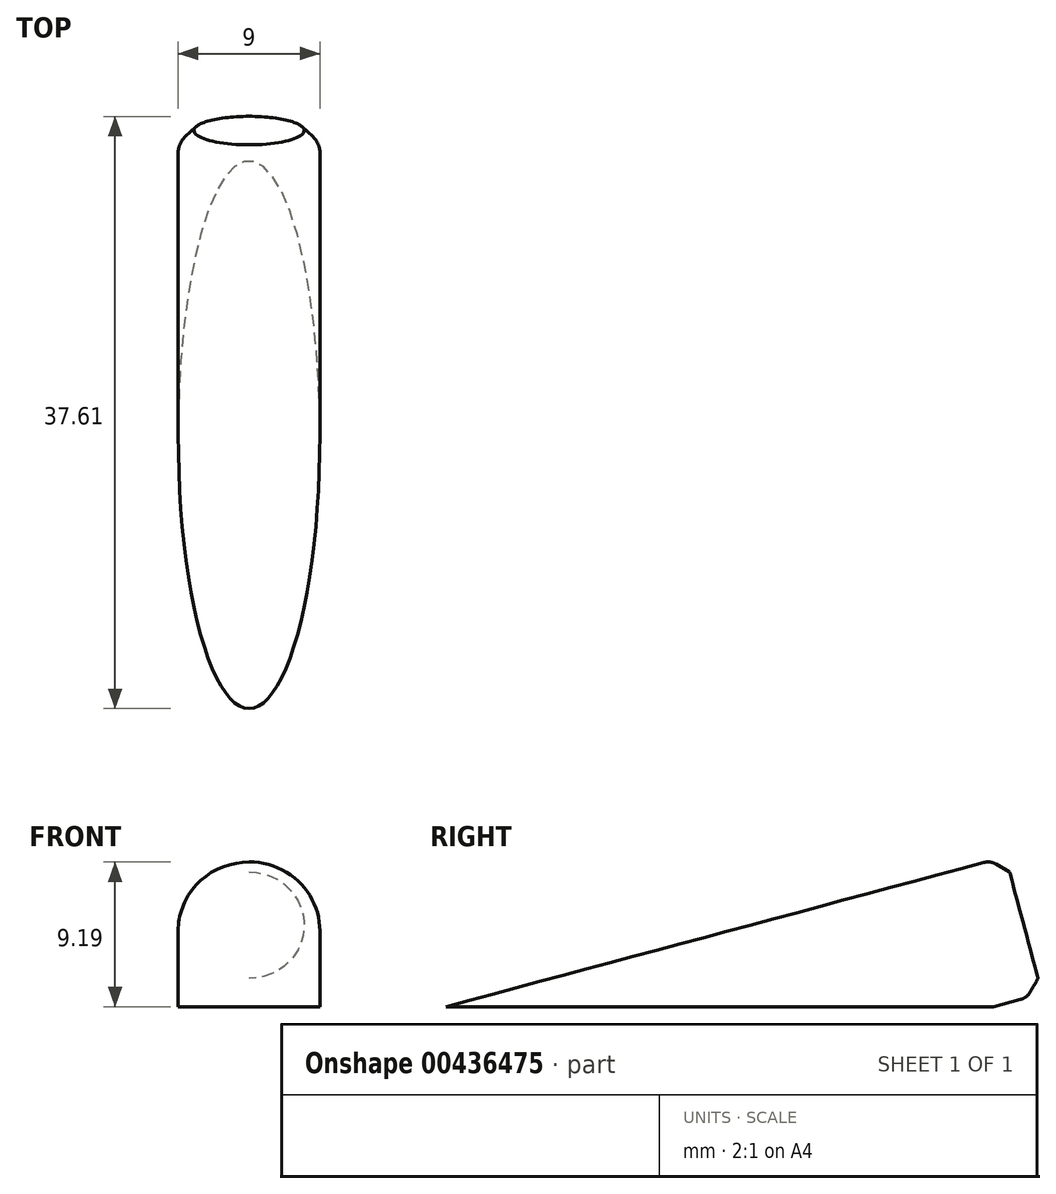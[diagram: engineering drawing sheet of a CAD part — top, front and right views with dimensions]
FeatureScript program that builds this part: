
annotation { "Feature Type Name" : "Feature", "Feature Type Description" : "" }
export const myFeature = defineFeature(function(context is Context, id is Id, definition is map)
    precondition{}
    {
        {
            var Q0;
            Q0=qCreatedBy(makeId("Top.planeOp"),FACE);
            var sketch = newSketch(context, id + "F0", { "sketchPlane" : qUnion([Q0])});
            skLineSegment(sketch, "E0", {"start": v(-35, 0) * mm, "end": v(35, 0) * mm});
            skSolve(sketch);
        }
        {
            var Q0;
            Q0=sQuery(id+"F0.wireOp",EDGE,"E0");
            cPlane(context, id + "F1", {"entities" : qUnion([Q0]), "cplaneType" : CPlaneType.LINE_ANGLE, "offset" : 25 * mm, "angle" : 15 * degree, "width" : 150 * mm, "height" : 150 * mm});
        }
        {
            var Q0;
            Q0=qCreatedBy(id+"F1.planeOp",FACE);
            var sketch = newSketch(context, id + "F2", { "sketchPlane" : qUnion([Q0])});
            skCircle(sketch, "E1", {"center": v(0, 0) * mm, "radius": 4.5 * mm});
            skSolve(sketch);
        }
        {
            var Q0;
            Q0=qSketchRegion(id+"F2",true);
            extrude(context, id + "F3", {"entities" : qUnion([Q0]), "endBound" : BoundingType.SYMMETRIC, "depth" : 40 * mm});
        }
        {
            var Q0;
            Q0=qCreatedBy(makeId("Top.planeOp"),FACE);
            var sketch = newSketch(context, id + "F4", { "sketchPlane" : qUnion([Q0])});
            skLineSegment(sketch, "E2.bottom", {"start": v(12.42, 30.4) * mm, "end": v(-12.42, 30.4) * mm});
            skLineSegment(sketch, "E2.top", {"start": v(12.42, -30.4) * mm, "end": v(-12.42, -30.4) * mm});
            skLineSegment(sketch, "E2.left", {"start": v(12.42, 30.4) * mm, "end": v(12.42, -30.4) * mm});
            skLineSegment(sketch, "E2.right", {"start": v(-12.42, 30.4) * mm, "end": v(-12.42, -30.4) * mm});
            skPoint(sketch, "E2.middle", {"position": v(0, 0) * mm});
            skLineSegment(sketch, "E3", {"start": v(0, 0) * mm, "end": v(0, 17) * mm, "construction": true});
            skSolve(sketch);
        }
        {
            var Q0;
            Q0=qSketchRegion(id+"F4",true);
            extrude(context, id + "F5", {"entities" : qUnion([Q0]), "operationType" : NewBodyOperationType.REMOVE, "oppositeDirection" : true, "depth" : 25 * mm});
        }
        {
            var Q0;
            Q0=makeQuery(id+"F5.boolean.opBoolean","COPY",FACE,{"derivedFrom":makeQuery(id+"F5.opExtrude","CAP_FACE",FACE,{"disambiguationData":[OSD([sQuery(id+"F4.wireOp",EDGE,"E2.bottom"),sQuery(id+"F4.wireOp",EDGE,"E2.top"),sQuery(id+"F4.wireOp",EDGE,"E2.left"),sQuery(id+"F4.wireOp",EDGE,"E2.right")])],"isStart":true})});
            var sketch = newSketch(context, id + "F6", { "sketchPlane" : qUnion([Q0])});
            skFitSpline(sketch, "E4.0", {"points": [v(0.6, 19.35) * mm, v(0, 19.4) * mm, v(-0.6, 19.35) * mm, v(-1.35, 19.13) * mm, v(-2.14, 18.66) * mm, v(-2.85, 17.95) * mm, v(-3.43, 17.14) * mm, v(-3.93, 16.23) * mm, v(-4.37, 15.2) * mm, v(-4.77, 14.06) * mm, v(-5.24, 12.4) * mm, v(-5.64, 10.53) * mm, v(-5.96, 8.48) * mm, v(-6.22, 6.34) * mm, v(-6.4, 4.08) * mm, v(-6.48, 1.76) * mm, v(-6.5, 0) * mm, v(-6.48, -1.76) * mm, v(-6.4, -4.08) * mm, v(-6.22, -6.34) * mm, v(-5.96, -8.48) * mm, v(-5.64, -10.53) * mm, v(-5.24, -12.4) * mm, v(-4.77, -14.06) * mm, v(-4.37, -15.2) * mm, v(-3.93, -16.23) * mm, v(-3.43, -17.14) * mm, v(-2.85, -17.95) * mm, v(-2.14, -18.66) * mm, v(-1.35, -19.13) * mm, v(-0.6, -19.35) * mm, v(0, -19.4) * mm, v(0.6, -19.35) * mm, v(1.35, -19.13) * mm, v(2.14, -18.66) * mm, v(2.85, -17.95) * mm, v(3.43, -17.14) * mm, v(3.93, -16.23) * mm, v(4.37, -15.2) * mm, v(4.77, -14.06) * mm, v(5.24, -12.4) * mm, v(5.64, -10.53) * mm, v(5.96, -8.48) * mm, v(6.22, -6.34) * mm, v(6.4, -4.08) * mm, v(6.48, -1.76) * mm, v(6.5, 0) * mm, v(6.48, 1.76) * mm, v(6.4, 4.08) * mm, v(6.22, 6.34) * mm, v(5.96, 8.48) * mm, v(5.64, 10.53) * mm, v(5.24, 12.4) * mm, v(4.77, 14.06) * mm, v(4.37, 15.2) * mm, v(3.93, 16.23) * mm, v(3.43, 17.14) * mm, v(2.85, 17.95) * mm, v(2.14, 18.66) * mm, v(1.35, 19.13) * mm, v(0.6, 19.35) * mm, v(0, 19.4) * mm, v(-0.6, 19.35) * mm, v(0.6, 19.35) * mm]});
            skSolve(sketch);
        }
        {
            var Q0;
            Q0=makeQuery(id+"F3.opExtrude","CAP_EDGE",EDGE,{"disambiguationData":[OSD([sQuery(id+"F2.wireOp",EDGE,"E1")])],"isStart":false});
            chamfer(context, id + "F7", {"entities" : qUnion([Q0]), "width" : 1 * mm, "tangentPropagation" : true});
        }
        {
            var Q0;
            {var subQ0=sQuery(id+"F2.wireOp",EDGE,"E1");Q0=makeQuery(id+"F7.opChamfer","BLEND_EDGE",EDGE,{"blendedFrom":[makeQuery(id+"F3.opExtrude","CAP_EDGE",EDGE,{"disambiguationData":[OSD([subQ0])],"isStart":false}),makeQuery(id+"F3.opExtrude","SWEPT_FACE",FACE,{"disambiguationData":[OSD([subQ0])]})],"blendedInto":[makeQuery(id+"F3.opExtrude","SWEPT_FACE",FACE,{"disambiguationData":[OSD([subQ0])]})]});}
            fillet(context, id + "F8", {"entities" : qUnion([Q0]), "radius" : 1 * mm, "tangentPropagation" : true, "allowEdgeOverflow" : false});
        }
    });
